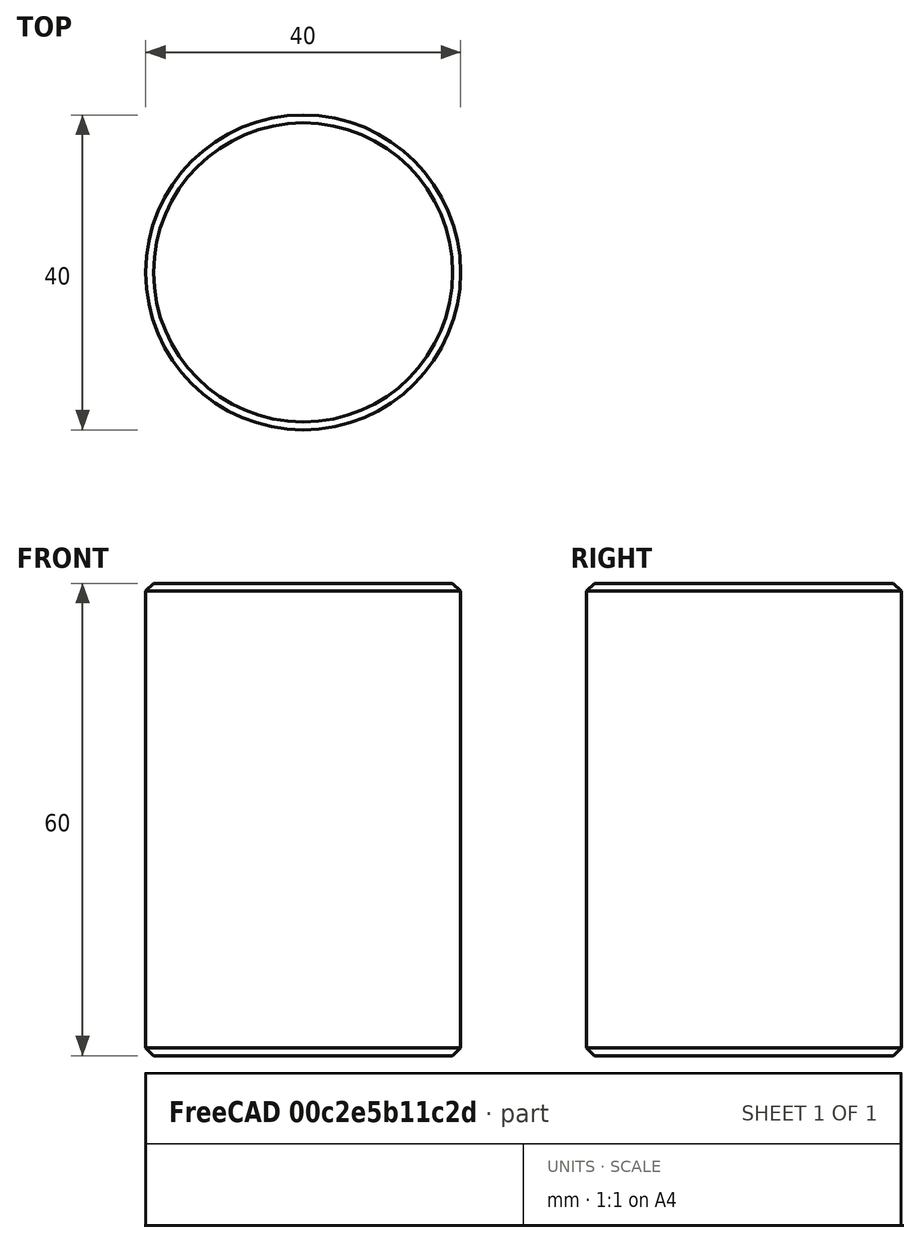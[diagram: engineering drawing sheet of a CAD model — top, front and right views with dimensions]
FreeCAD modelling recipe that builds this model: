
FCSTD DOCUMENT  (FreeCAD 1.0R39319 (Git))
Label: p2
License: All rights reserved
objects: Sketcher::SketchObject×1, PartDesign::Pad×1, PartDesign::Thickness×1, PartDesign::Chamfer×1, PartDesign::Body×1
note: 12 computed .brp shape members not serialized (recipe doc carries the construction recipe); baked Part::Feature solids carry a one-line shape summary decoded from their .brp

FEATURE [Sketcher::SketchObject] Sketch
  ArcFitTolerance = 1e-06
  AttachmentSupport = -> [XY_Plane]
  FullyConstrained = true
  MakeInternals = false
  MapMode = 5
  sketch-geometry (1):
    g0: Circle CenterX=0 CenterY=0 CenterZ=0 NormalX=0 NormalY=0 NormalZ=1 AngleXU=0 Radius=20
  constraints (2):
    c: Diameter(g0) = 40
    c: Coincident(g0,g-1)
FEATURE [PartDesign::Pad] Pad
  Direction = (0,0,1)
  Length = 60
  Length2 = 10
  Profile = -> Sketch
  ReferenceAxis = -> Sketch [N_Axis]
  Refine = true
  Suppressed = false
  Type = 0
FEATURE [PartDesign::Thickness] Thickness
  Base = -> Pad [Face2]
  BaseFeature = -> Pad
  Intersection = false
  Join = 0
  Mode = 0
  Refine = true
  Reversed = true
  SupportTransform = false
  Suppressed = false
  Value = 5
FEATURE [PartDesign::Chamfer] Chamfer
  Angle = 45
  Base = -> Pad [Edge1,Edge2,Edge3]
  BaseFeature = -> Pad
  ChamferType = 0
  FlipDirection = false
  Refine = true
  Size = 1
  Size2 = 1
  SupportTransform = false
  Suppressed = false
  UseAllEdges = true
FEATURE [PartDesign::Body] Body
  AllowCompound = false
  Group = -> [Sketch,Pad,Thickness,Chamfer]
  Origin = -> Origin
  Tip = -> Chamfer
